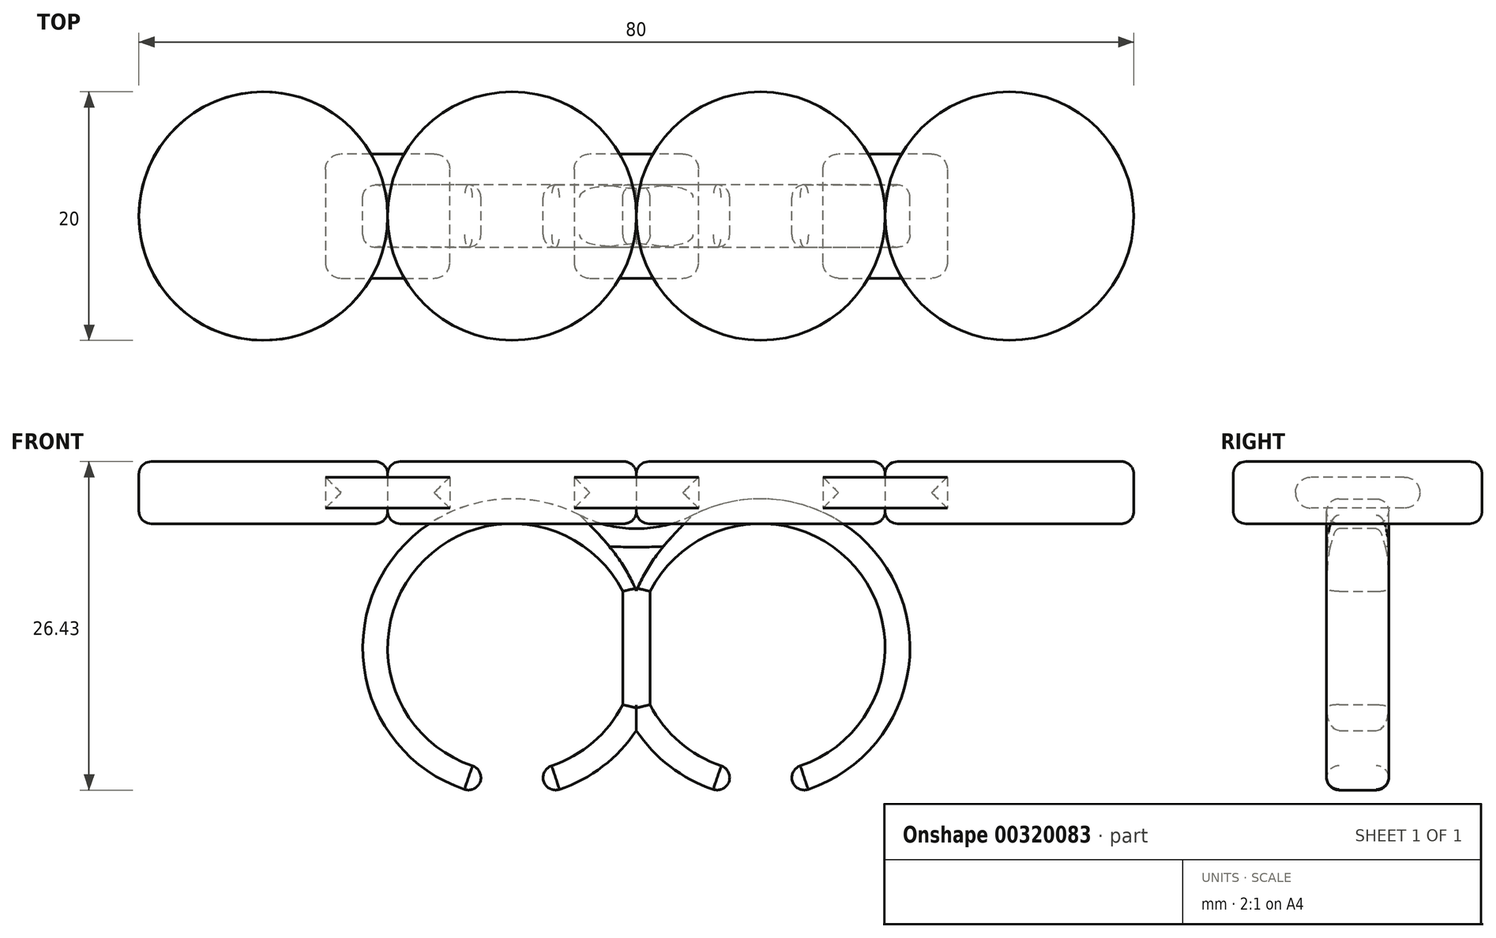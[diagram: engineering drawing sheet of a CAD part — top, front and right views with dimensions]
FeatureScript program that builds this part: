
annotation { "Feature Type Name" : "Feature", "Feature Type Description" : "" }
export const myFeature = defineFeature(function(context is Context, id is Id, definition is map)
    precondition{}
    {
        {
            var Q0;
            Q0=qCreatedBy(makeId("Top.planeOp"),FACE);
            var sketch = newSketch(context, id + "F0", { "sketchPlane" : qUnion([Q0])});
            skLineSegment(sketch, "E0", {"start": v(0, 0) * mm, "end": v(40, 0) * mm});
            skPoint(sketch, "E1", {"position": v(20, 0) * mm});
            skPoint(sketch, "E2", {"position": v(-20, 0) * mm});
            skPoint(sketch, "E3", {"position": v(30, 0) * mm});
            skPoint(sketch, "E4", {"position": v(10, 0) * mm});
            skCircle(sketch, "E5", {"center": v(30, 0) * mm, "radius": 10 * mm});
            skCircle(sketch, "E6", {"center": v(10, 0) * mm, "radius": 10 * mm});
            skCircle(sketch, "E7.MirrorC", {"center": v(-10, 0) * mm, "radius": 10 * mm});
            skCircle(sketch, "E8.MirrorC", {"center": v(-30, 0) * mm, "radius": 10 * mm});
            skLineSegment(sketch, "E9.MirrorCS", {"start": v(0, 0) * mm, "end": v(-40, 0) * mm});
            skSolve(sketch);
        }
        {
            var Q0;
            Q0 = qSketchRegion(id + "F0", true);
            extrude(context, id + "F1", {"entities" : qUnion([Q0]), "depth" : 5 * mm});
        }
        {
            var Q0;
            Q0=qCreatedBy(makeId("Top.planeOp"),FACE);
            var sketch = newSketch(context, id + "F2", { "sketchPlane" : qUnion([Q0])});
            skLineSegment(sketch, "E10", {"start": v(-20, 5) * mm, "end": v(-15, 5) * mm});
            skLineSegment(sketch, "E11.MirrorCS", {"start": v(-20, 5) * mm, "end": v(-25, 5) * mm});
            skLineSegment(sketch, "E12.MirrorCS", {"start": v(-20, -5) * mm, "end": v(-15, -5) * mm});
            skLineSegment(sketch, "E13.MirrorCS", {"start": v(-20, -5) * mm, "end": v(-25, -5) * mm});
            skLineSegment(sketch, "E14", {"start": v(-25, 5) * mm, "end": v(-25, -5) * mm});
            skLineSegment(sketch, "E15", {"start": v(-15, -5) * mm, "end": v(-15, 5) * mm});
            skLineSegment(sketch, "E16.MirrorCS", {"start": v(20, 5) * mm, "end": v(15, 5) * mm});
            skLineSegment(sketch, "E17.MirrorCS", {"start": v(20, 5) * mm, "end": v(25, 5) * mm});
            skLineSegment(sketch, "E18.MirrorCS", {"start": v(25, 5) * mm, "end": v(25, -5) * mm});
            skLineSegment(sketch, "E19.MirrorCS", {"start": v(15, -5) * mm, "end": v(15, 5) * mm});
            skLineSegment(sketch, "E20.MirrorCS", {"start": v(20, -5) * mm, "end": v(15, -5) * mm});
            skLineSegment(sketch, "E21.MirrorCS", {"start": v(20, -5) * mm, "end": v(25, -5) * mm});
            skLineSegment(sketch, "E22", {"start": v(0, 5) * mm, "end": v(5, 5) * mm});
            skLineSegment(sketch, "E23.MirrorCS", {"start": v(0, 5) * mm, "end": v(-5, 5) * mm});
            skLineSegment(sketch, "E24.MirrorCS", {"start": v(0, -5) * mm, "end": v(5, -5) * mm});
            skLineSegment(sketch, "E25.MirrorCS", {"start": v(0, -5) * mm, "end": v(-5, -5) * mm});
            skLineSegment(sketch, "E26", {"start": v(-5, 5) * mm, "end": v(-5, -5) * mm});
            skLineSegment(sketch, "E27", {"start": v(5, -5) * mm, "end": v(5, 5) * mm});
            skSolve(sketch);
        }
        {
            var Q0;
            Q0 = qSketchRegion(id + "F2", true);
            extrude(context, id + "F3", {"entities" : qUnion([Q0]), "depth" : 3.75 * mm, "hasSecondDirection" : true, "secondDirectionOppositeDirection" : false, "secondDirectionDepth" : 1.25 * mm});
        }
        {
            var Q0;
            Q0=qCreatedBy(makeId("Front.planeOp"),FACE);
            var sketch = newSketch(context, id + "F4", { "sketchPlane" : qUnion([Q0])});
            skLineSegment(sketch, "E28", {"start": v(0, 0) * mm, "end": v(10, 0) * mm});
            skLineSegment(sketch, "E29", {"start": v(10, 0) * mm, "end": v(10, -10) * mm});
            skArc(sketch, "E30", {"start": v(1.1, -14.56) * mm, "mid": v(3.75, -17.8) * mm, "end": v(7.5, -19.68) * mm});
            skArc(sketch, "E31.0", {"start": v(0, -16.63) * mm, "mid": v(3.25, -19.92) * mm, "end": v(7.5, -21.74) * mm});
            skArc(sketch, "E32.MirrorC", {"start": v(0, -16.63) * mm, "mid": v(-3.25, -19.92) * mm, "end": v(-7.5, -21.74) * mm});
            skArc(sketch, "E33.MirrorC", {"start": v(-1.1, -14.56) * mm, "mid": v(-3.75, -17.8) * mm, "end": v(-7.5, -19.68) * mm});
            skLineSegment(sketch, "E34", {"start": v(1.1, -14.56) * mm, "end": v(1.1, -5.44) * mm});
            skLineSegment(sketch, "E35.MirrorCS", {"start": v(-1.1, -14.56) * mm, "end": v(-1.1, -5.44) * mm});
            skLineSegment(sketch, "E36.0", {"start": v(-12.5, -19.68) * mm, "end": v(-12.5, -21.74) * mm});
            skLineSegment(sketch, "E37.0", {"start": v(-7.5, -19.68) * mm, "end": v(-7.5, -21.74) * mm});
            skArc(sketch, "E38.trimOffspring", {"start": v(-12.5, -19.68) * mm, "mid": v(-17.8, -3.75) * mm, "end": v(-1.1, -5.44) * mm});
            skArc(sketch, "E39.trimOffspring", {"start": v(-12.5, -21.74) * mm, "mid": v(-19.92, -3.25) * mm, "end": v(0, -3.37) * mm});
            skLineSegment(sketch, "E40.MirrorCS", {"start": v(7.5, -19.68) * mm, "end": v(7.5, -21.74) * mm});
            skLineSegment(sketch, "E41.MirrorCS", {"start": v(12.5, -19.68) * mm, "end": v(12.5, -21.74) * mm});
            skArc(sketch, "E42.trimOffspring", {"start": v(12.5, -19.68) * mm, "mid": v(17.8, -3.75) * mm, "end": v(1.1, -5.44) * mm});
            skArc(sketch, "E43.trimOffspring", {"start": v(12.5, -21.74) * mm, "mid": v(19.92, -3.25) * mm, "end": v(0, -3.37) * mm});
            skSolve(sketch);
        }
        {
            var Q0;
            Q0 = qSketchRegion(id + "F4", true);
            extrude(context, id + "F5", {"entities" : qUnion([Q0]), "depth" : 2.5 * mm, "hasSecondDirection" : true, "secondDirectionOppositeDirection" : true, "secondDirectionDepth" : 2.5 * mm});
        }
        {
            var Q0;
            Q0=makeQuery(id+"F5.opExtrude","SWEPT_FACE",FACE,{"disambiguationData":[OSD([sQuery(id+"F4.wireOp",EDGE,"E41.MirrorCS")])]});
            var Q1;
            Q1=makeQuery(id+"F5.opExtrude","SWEPT_FACE",FACE,{"disambiguationData":[OSD([sQuery(id+"F4.wireOp",EDGE,"E37.0")])]});
            var Q2;
            Q2=makeQuery(id+"F5.opExtrude","SWEPT_FACE",FACE,{"disambiguationData":[OSD([sQuery(id+"F4.wireOp",EDGE,"E36.0")])]});
            var Q3;
            Q3=makeQuery(id+"F5.opExtrude","SWEPT_FACE",FACE,{"disambiguationData":[OSD([sQuery(id+"F4.wireOp",EDGE,"E40.MirrorCS")])]});
            fillet(context, id + "F6", {"entities" : qUnion([Q0, Q1, Q2, Q3]), "radius" : 1 * mm, "tangentPropagation" : true, "allowEdgeOverflow" : false});
        }
        {
            var Q0;
            Q0=makeQuery(id+"F5.opExtrude","CAP_FACE",FACE,{"disambiguationData":[OSD([sQuery(id+"F4.wireOp",EDGE,"E31.0"),sQuery(id+"F4.wireOp",EDGE,"E32.MirrorC"),sQuery(id+"F4.wireOp",EDGE,"E33.MirrorC"),sQuery(id+"F4.wireOp",EDGE,"E30"),sQuery(id+"F4.wireOp",EDGE,"E34"),sQuery(id+"F4.wireOp",EDGE,"E35.MirrorCS"),sQuery(id+"F4.wireOp",EDGE,"E36.0"),sQuery(id+"F4.wireOp",EDGE,"E37.0"),sQuery(id+"F4.wireOp",EDGE,"E38.trimOffspring"),sQuery(id+"F4.wireOp",EDGE,"E39.trimOffspring"),sQuery(id+"F4.wireOp",EDGE,"E40.MirrorCS"),sQuery(id+"F4.wireOp",EDGE,"E41.MirrorCS"),sQuery(id+"F4.wireOp",EDGE,"E43.trimOffspring"),sQuery(id+"F4.wireOp",EDGE,"E42.trimOffspring")])],"isStart":true});
            var Q1;
            Q1=makeQuery(id+"F5.opExtrude","CAP_FACE",FACE,{"disambiguationData":[OSD([sQuery(id+"F4.wireOp",EDGE,"E31.0"),sQuery(id+"F4.wireOp",EDGE,"E32.MirrorC"),sQuery(id+"F4.wireOp",EDGE,"E33.MirrorC"),sQuery(id+"F4.wireOp",EDGE,"E30"),sQuery(id+"F4.wireOp",EDGE,"E34"),sQuery(id+"F4.wireOp",EDGE,"E35.MirrorCS"),sQuery(id+"F4.wireOp",EDGE,"E36.0"),sQuery(id+"F4.wireOp",EDGE,"E37.0"),sQuery(id+"F4.wireOp",EDGE,"E38.trimOffspring"),sQuery(id+"F4.wireOp",EDGE,"E39.trimOffspring"),sQuery(id+"F4.wireOp",EDGE,"E40.MirrorCS"),sQuery(id+"F4.wireOp",EDGE,"E41.MirrorCS"),sQuery(id+"F4.wireOp",EDGE,"E43.trimOffspring"),sQuery(id+"F4.wireOp",EDGE,"E42.trimOffspring")])],"isStart":false});
            fillet(context, id + "F7", {"entities" : qUnion([Q0, Q1]), "radius" : 1 * mm, "tangentPropagation" : true, "allowEdgeOverflow" : false});
        }
        {
            var Q0;
            Q0=makeQuery(id+"F1.opExtrude","CAP_FACE",FACE,{"disambiguationData":[OSD([sQuery(id+"F0.wireOp",EDGE,"E7.MirrorC")])],"isStart":false});
            var Q1;
            Q1=makeQuery(id+"F1.opExtrude","CAP_FACE",FACE,{"disambiguationData":[OSD([sQuery(id+"F0.wireOp",EDGE,"E8.MirrorC")])],"isStart":false});
            var Q2;
            Q2=makeQuery(id+"F1.opExtrude","CAP_FACE",FACE,{"disambiguationData":[OSD([sQuery(id+"F0.wireOp",EDGE,"E6")])],"isStart":false});
            var Q3;
            Q3=makeQuery(id+"F1.opExtrude","CAP_FACE",FACE,{"disambiguationData":[OSD([sQuery(id+"F0.wireOp",EDGE,"E5")])],"isStart":false});
            fillet(context, id + "F8", {"entities" : qUnion([Q0, Q1, Q2, Q3]), "radius" : 1 * mm, "tangentPropagation" : true, "allowEdgeOverflow" : false});
        }
        {
            var Q0;
            Q0=makeQuery(id+"F1.opExtrude","CAP_FACE",FACE,{"disambiguationData":[OSD([sQuery(id+"F0.wireOp",EDGE,"E8.MirrorC")])],"isStart":true});
            var Q1;
            Q1=makeQuery(id+"F1.opExtrude","CAP_FACE",FACE,{"disambiguationData":[OSD([sQuery(id+"F0.wireOp",EDGE,"E7.MirrorC")])],"isStart":true});
            var Q2;
            Q2=makeQuery(id+"F1.opExtrude","CAP_FACE",FACE,{"disambiguationData":[OSD([sQuery(id+"F0.wireOp",EDGE,"E6")])],"isStart":true});
            var Q3;
            Q3=makeQuery(id+"F1.opExtrude","CAP_FACE",FACE,{"disambiguationData":[OSD([sQuery(id+"F0.wireOp",EDGE,"E5")])],"isStart":true});
            fillet(context, id + "F9", {"entities" : qUnion([Q0, Q1, Q2, Q3]), "radius" : 1 * mm, "tangentPropagation" : true, "allowEdgeOverflow" : false});
        }
        {
            var Q0;
            Q0=makeQuery(id+"F5.opExtrude","SWEPT_FACE",FACE,{"disambiguationData":[OSD([sQuery(id+"F4.wireOp",EDGE,"E39.trimOffspring")])]});
            var Q1;
            Q1=makeQuery(id+"F5.opExtrude","SWEPT_FACE",FACE,{"disambiguationData":[OSD([sQuery(id+"F4.wireOp",EDGE,"E43.trimOffspring")])]});
            fillet(context, id + "F10", {"entities" : qUnion([Q0, Q1]), "radius" : 10 * mm, "tangentPropagation" : true, "allowEdgeOverflow" : false});
        }
        {
            var Q0;
            Q0=makeQuery(id+"F3.opExtrude","SWEPT_FACE",FACE,{"disambiguationData":[OSD([sQuery(id+"F2.wireOp",EDGE,"E12.MirrorCS"),sQuery(id+"F2.wireOp",EDGE,"E13.MirrorCS")])]});
            var Q1;
            Q1=makeQuery(id+"F3.opExtrude","SWEPT_FACE",FACE,{"disambiguationData":[OSD([sQuery(id+"F2.wireOp",EDGE,"E24.MirrorCS"),sQuery(id+"F2.wireOp",EDGE,"E25.MirrorCS")])]});
            var Q2;
            Q2=makeQuery(id+"F3.opExtrude","SWEPT_FACE",FACE,{"disambiguationData":[OSD([sQuery(id+"F2.wireOp",EDGE,"E20.MirrorCS"),sQuery(id+"F2.wireOp",EDGE,"E21.MirrorCS")])]});
            var Q3;
            Q3=makeQuery(id+"F3.opExtrude","SWEPT_FACE",FACE,{"disambiguationData":[OSD([sQuery(id+"F2.wireOp",EDGE,"E16.MirrorCS"),sQuery(id+"F2.wireOp",EDGE,"E17.MirrorCS")])]});
            var Q4;
            Q4=makeQuery(id+"F3.opExtrude","SWEPT_FACE",FACE,{"disambiguationData":[OSD([sQuery(id+"F2.wireOp",EDGE,"E22"),sQuery(id+"F2.wireOp",EDGE,"E23.MirrorCS")])]});
            var Q5;
            Q5=makeQuery(id+"F3.opExtrude","SWEPT_FACE",FACE,{"disambiguationData":[OSD([sQuery(id+"F2.wireOp",EDGE,"E10"),sQuery(id+"F2.wireOp",EDGE,"E11.MirrorCS")])]});
            fillet(context, id + "F11", {"entities" : qUnion([Q0, Q1, Q2, Q3, Q4, Q5]), "radius" : 1.25 * mm, "tangentPropagation" : true, "allowEdgeOverflow" : false});
        }
    });
